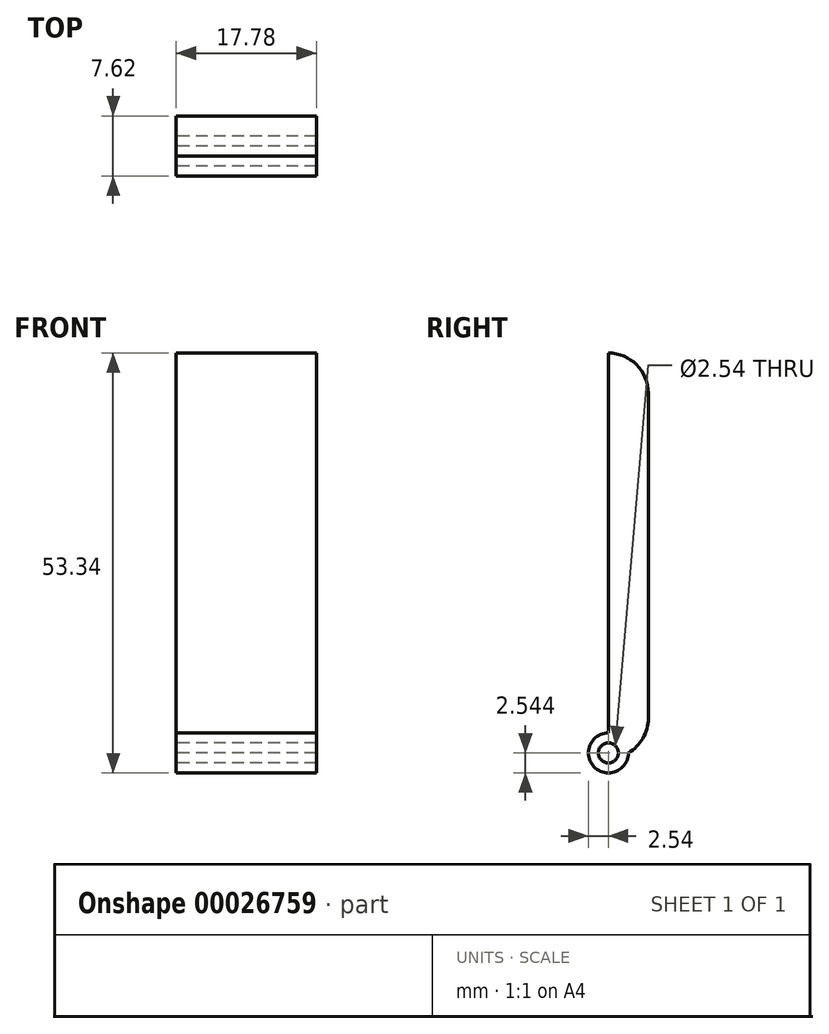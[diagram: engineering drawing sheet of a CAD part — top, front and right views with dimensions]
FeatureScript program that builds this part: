
annotation { "Feature Type Name" : "Feature", "Feature Type Description" : "" }
export const myFeature = defineFeature(function(context is Context, id is Id, definition is map)
    precondition{}
    {
        {
            var Q0;
            Q0=qCreatedBy(makeId("Right.planeOp"),FACE);
            var sketch = newSketch(context, id + "F0", { "sketchPlane" : qUnion([Q0])});
            skLineSegment(sketch, "E0.rect.bottom", {"start": v(2.54, -18.65) * mm, "end": v(0, -18.65) * mm});
            skLineSegment(sketch, "E0.rect.top", {"start": v(2.54, 32.15) * mm, "end": v(-2.54, 32.15) * mm});
            skLineSegment(sketch, "E0.rect.left", {"start": v(2.54, -18.65) * mm, "end": v(2.54, 32.15) * mm});
            skLineSegment(sketch, "E0.rect.right", {"start": v(-2.54, -16.1) * mm, "end": v(-2.54, 32.15) * mm});
            skPoint(sketch, "E0.rect.middle", {"position": v(0, 6.75) * mm});
            skArc(sketch, "E1", {"start": v(-2.54, -16.1) * mm, "mid": v(-4.34, -20.44) * mm, "end": v(0, -18.65) * mm});
            skCircle(sketch, "E2", {"center": v(-2.54, -18.65) * mm, "radius": 1.27 * mm});
            skSolve(sketch);
        }
        {
            var Q0;
            Q0=makeQuery(id+"F0.imprint","IMPRINT",FACE,{"disambiguationData":[TD([[makeQuery(id+"F0.imprint","IMPRINT",EDGE,{"derivedFrom":sQuery(id+"F0.wireOp",EDGE,"E0.rect.bottom")}),-1.0]])]});
            extrude(context, id + "F1", {"entities" : qUnion([Q0]), "depth" : 17.78 * mm});
        }
        {
            var Q0;
            Q0=makeQuery(id+"F1.opExtrude","SWEPT_EDGE",EDGE,{"disambiguationData":[OSD([sQuery(id+"F0.wireOp",EDGE,"E0.rect.bottom"),sQuery(id+"F0.wireOp",EDGE,"E0.rect.left")])]});
            var Q1;
            Q1=makeQuery(id+"F1.opExtrude","SWEPT_EDGE",EDGE,{"disambiguationData":[OSD([sQuery(id+"F0.wireOp",EDGE,"E0.rect.top"),sQuery(id+"F0.wireOp",EDGE,"E0.rect.left")])]});
            fillet(context, id + "F2", {"entities" : qUnion([Q0, Q1]), "radius" : 5.08 * mm, "tangentPropagation" : true, "allowEdgeOverflow" : false});
        }
    });
